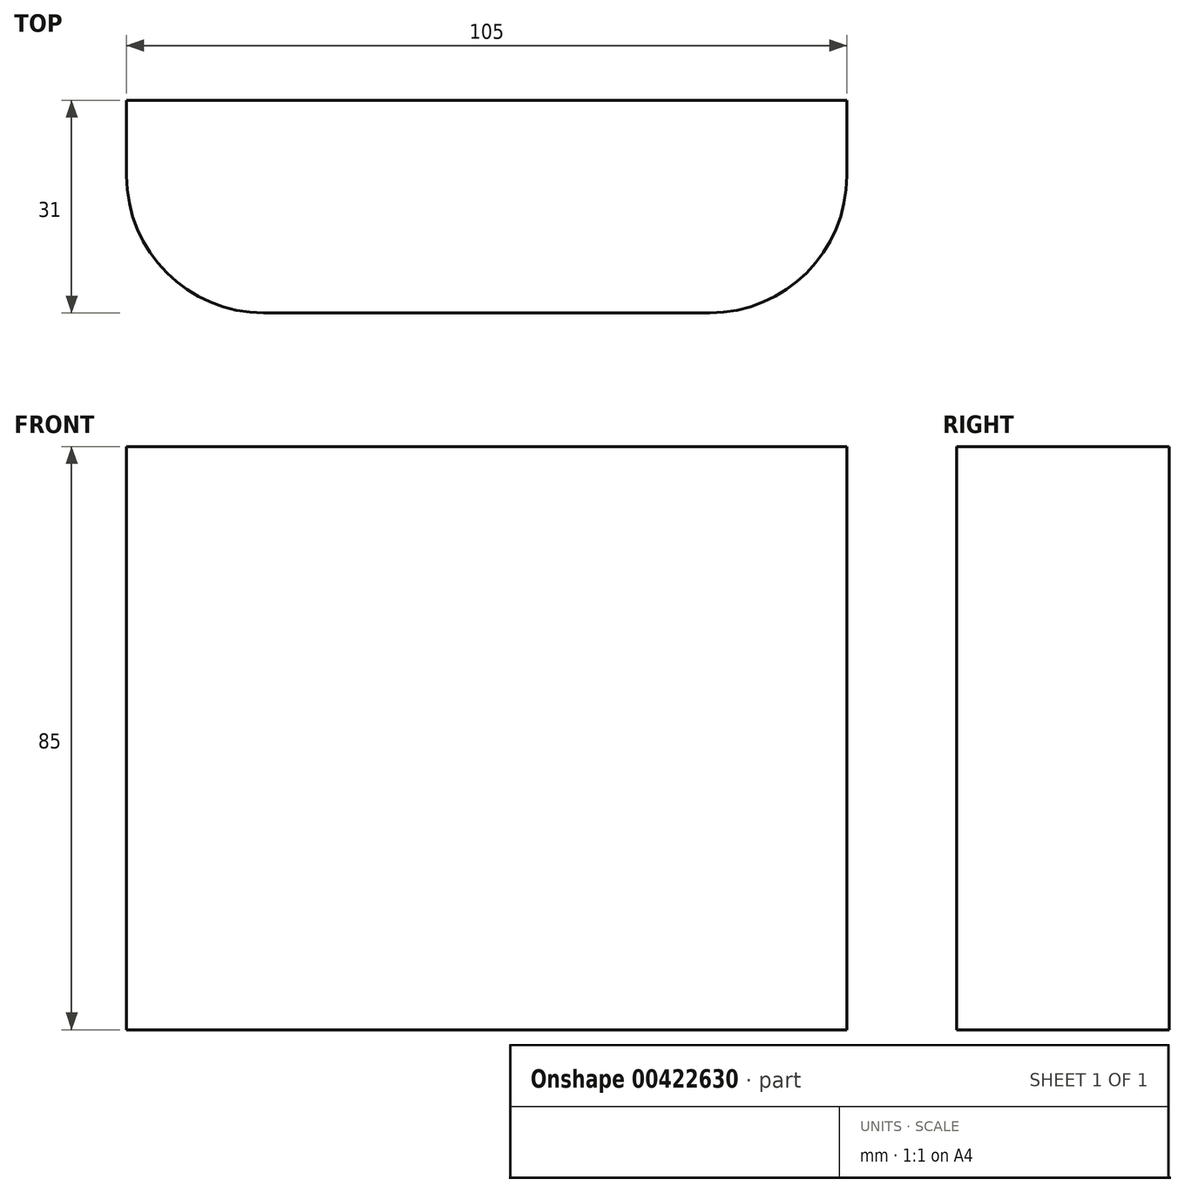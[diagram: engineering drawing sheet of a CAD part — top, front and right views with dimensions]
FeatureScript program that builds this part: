
annotation { "Feature Type Name" : "Feature", "Feature Type Description" : "" }
export const myFeature = defineFeature(function(context is Context, id is Id, definition is map)
    precondition{}
    {
        {
            var Q0;
            Q0=qCreatedBy(makeId("Front.planeOp"),FACE);
            var sketch = newSketch(context, id + "F0", { "sketchPlane" : qUnion([Q0])});
            skLineSegment(sketch, "E0.bottom", {"start": v(0, 0) * mm, "end": v(105, 0) * mm});
            skLineSegment(sketch, "E0.top", {"start": v(0, 85) * mm, "end": v(105, 85) * mm});
            skLineSegment(sketch, "E0.left", {"start": v(0, 0) * mm, "end": v(0, 85) * mm});
            skLineSegment(sketch, "E0.right", {"start": v(105, 0) * mm, "end": v(105, 85) * mm});
            skSolve(sketch);
        }
        {
            var Q0;
            Q0=makeQuery(id+"F0.imprint","IMPRINT",FACE,{"disambiguationData":[TD([[makeQuery(id+"F0.imprint","IMPRINT",EDGE,{"derivedFrom":sQuery(id+"F0.wireOp",EDGE,"E0.bottom")}),1.0]])]});
            extrude(context, id + "F1", {"entities" : qUnion([Q0]), "depth" : 31 * mm});
        }
        {
            var Q0;
            Q0=makeQuery(id+"F1.opExtrude","CAP_EDGE",EDGE,{"disambiguationData":[OSD([sQuery(id+"F0.wireOp",EDGE,"E0.right")])],"isStart":false});
            var Q1;
            Q1=makeQuery(id+"F1.opExtrude","CAP_EDGE",EDGE,{"disambiguationData":[OSD([sQuery(id+"F0.wireOp",EDGE,"E0.left")])],"isStart":false});
            fillet(context, id + "F2", {"entities" : qUnion([Q0, Q1]), "radius" : 20 * mm, "tangentPropagation" : true, "allowEdgeOverflow" : false});
        }
    });
